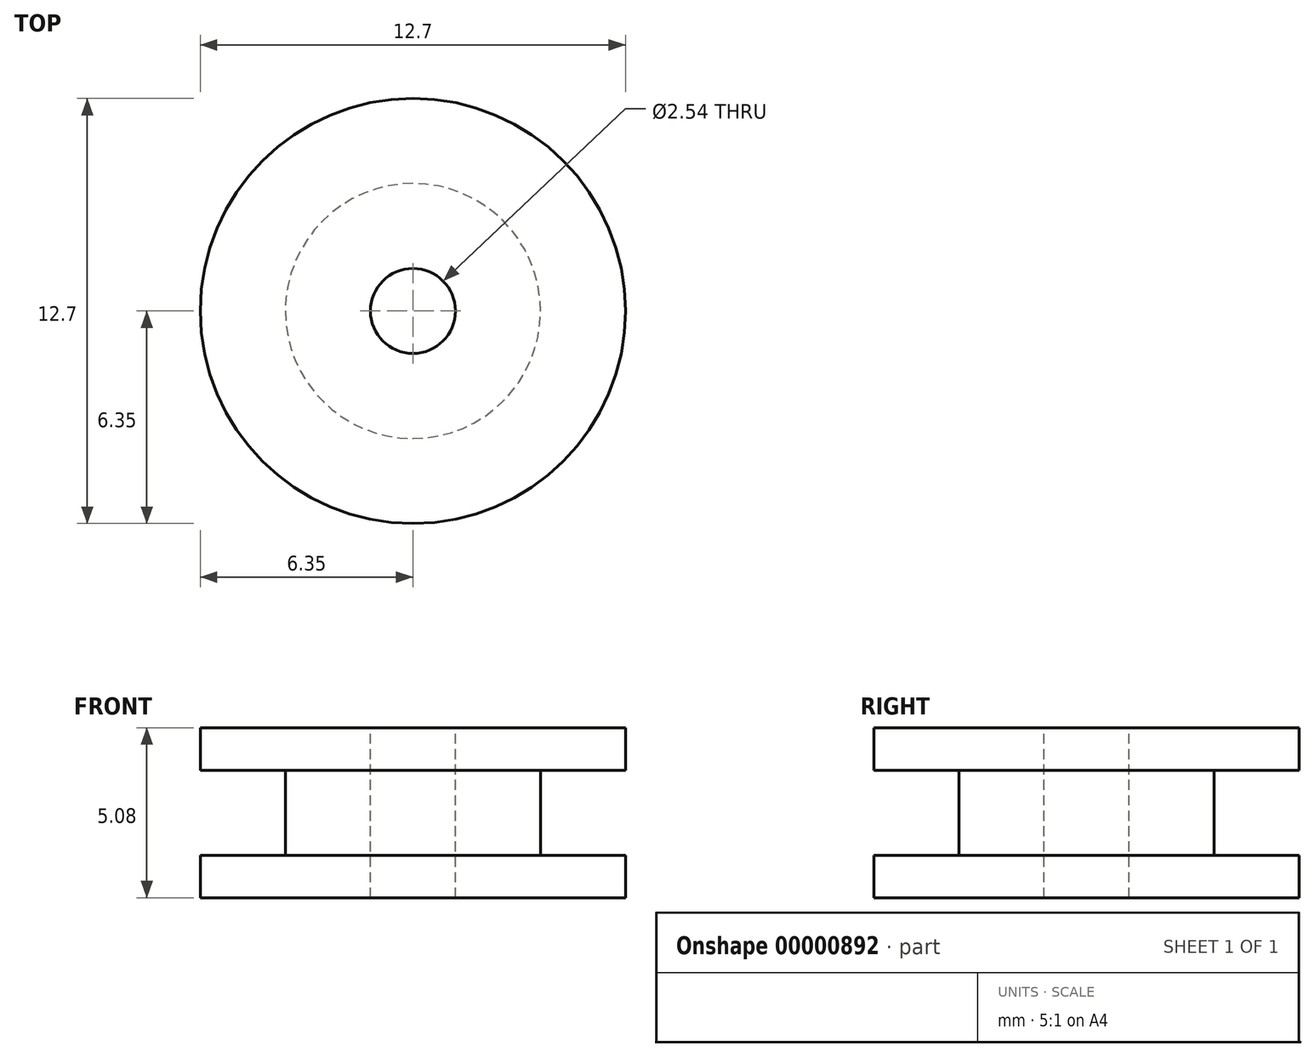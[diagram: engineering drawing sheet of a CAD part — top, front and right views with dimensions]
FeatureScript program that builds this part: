
annotation { "Feature Type Name" : "Feature", "Feature Type Description" : "" }
export const myFeature = defineFeature(function(context is Context, id is Id, definition is map)
    precondition{}
    {
        {
            var Q0;
            Q0=qCreatedBy(makeId("Top.planeOp"),FACE);
            var sketch = newSketch(context, id + "F0", { "sketchPlane" : qUnion([Q0])});
            skCircle(sketch, "E0", {"center": v(0, 0) * mm, "radius": 3.81 * mm});
            skSolve(sketch);
        }
        {
            var Q0;
            Q0=makeQuery(id+"F0.imprint","IMPRINT",FACE,{"disambiguationData":[TD([[makeQuery(id+"F0.imprint","IMPRINT",EDGE,{"derivedFrom":sQuery(id+"F0.wireOp",EDGE,"E0")}),1.0]])]});
            extrude(context, id + "F1", {"entities" : qUnion([Q0]), "depth" : 2.54 * mm});
        }
        {
            var Q0;
            Q0=makeQuery(id+"F1.opExtrude","CAP_FACE",FACE,{"disambiguationData":[OSD([sQuery(id+"F0.wireOp",EDGE,"E0")])],"isStart":true});
            var sketch = newSketch(context, id + "F2", { "sketchPlane" : qUnion([Q0])});
            skCircle(sketch, "E1", {"center": v(0, 0) * mm, "radius": 6.35 * mm});
            skSolve(sketch);
        }
        {
            var Q0;
            Q0=makeQuery(id+"F2.imprint","IMPRINT",FACE,{"disambiguationData":[TD([[makeQuery(id+"F2.imprint","IMPRINT",EDGE,{"derivedFrom":sQuery(id+"F2.wireOp",EDGE,"E1")}),1.0]])]});
            var Q1;
            Q1=makeQuery(id+"F2.imprint","IMPRINT",FACE,{"disambiguationData":[TD([[makeQuery(id+"F2.imprint","IMPRINT",EDGE,{"derivedFrom":makeQuery(id+"F1.opExtrude","CAP_EDGE",EDGE,{"disambiguationData":[OSD([sQuery(id+"F0.wireOp",EDGE,"E0")])],"isStart":true})}),-1.0]])]});
            extrude(context, id + "F3", {"entities" : qUnion([Q0, Q1]), "operationType" : NewBodyOperationType.ADD, "depth" : 1.27 * mm});
        }
        {
            var Q0;
            Q0=makeQuery(id+"F1.opExtrude","CAP_FACE",FACE,{"disambiguationData":[OSD([sQuery(id+"F0.wireOp",EDGE,"E0")])],"isStart":false});
            var sketch = newSketch(context, id + "F4", { "sketchPlane" : qUnion([Q0])});
            skCircle(sketch, "E2", {"center": v(0, 0) * mm, "radius": 6.35 * mm});
            skSolve(sketch);
        }
        {
            var Q0;
            Q0=makeQuery(id+"F4.imprint","IMPRINT",FACE,{"disambiguationData":[TD([[makeQuery(id+"F4.imprint","IMPRINT",EDGE,{"derivedFrom":sQuery(id+"F4.wireOp",EDGE,"E2")}),1.0]])]});
            var Q1;
            Q1=makeQuery(id+"F4.imprint","IMPRINT",FACE,{"disambiguationData":[TD([[makeQuery(id+"F4.imprint","IMPRINT",EDGE,{"derivedFrom":makeQuery(id+"F1.opExtrude","CAP_EDGE",EDGE,{"disambiguationData":[OSD([sQuery(id+"F0.wireOp",EDGE,"E0")])],"isStart":false})}),1.0]])]});
            extrude(context, id + "F5", {"entities" : qUnion([Q0, Q1]), "operationType" : NewBodyOperationType.ADD, "depth" : 1.27 * mm});
        }
        {
            var Q0;
            Q0=makeQuery(id+"F5.opExtrude","CAP_FACE",FACE,{"disambiguationData":[OSD([sQuery(id+"F4.wireOp",EDGE,"E2")])],"isStart":false});
            var sketch = newSketch(context, id + "F6", { "sketchPlane" : qUnion([Q0])});
            skCircle(sketch, "E3", {"center": v(0, 0) * mm, "radius": 1.27 * mm});
            skSolve(sketch);
        }
        {
            var Q0;
            Q0=makeQuery(id+"F6.imprint","IMPRINT",FACE,{"disambiguationData":[TD([[makeQuery(id+"F6.imprint","IMPRINT",EDGE,{"derivedFrom":sQuery(id+"F6.wireOp",EDGE,"E3")}),1.0]])]});
            extrude(context, id + "F7", {"entities" : qUnion([Q0]), "operationType" : NewBodyOperationType.REMOVE, "endBound" : BoundingType.THROUGH_ALL, "oppositeDirection" : true, "depth" : 25.4 * mm});
        }
    });
